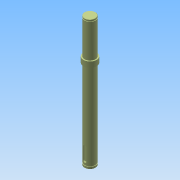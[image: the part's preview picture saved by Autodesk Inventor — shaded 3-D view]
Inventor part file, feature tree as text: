
AUTODESK INVENTOR PART (.ipt)
format: ipt  version: 2015 (Build 190159000, 159)  size: 131,072 bytes
history: native  units: mm
features: sketch x5, extrude x3, plane x2, revolve x2, chamfer x2
ambient origin geometry x8: Origin, YZ Plane, XZ Plane, XY Plane, X Axis, Y Axis, Z Axis, Center Point
bodies: 实体1 (feature_tree)
feature tree (14):
  extrude  "拉伸1"  Depth=237.2mm TaperAngle=0.0deg
  plane  "工作平面1"
  extrude  "拉伸2"  Depth=22.0mm
  revolve  "旋转1"  [1 undecoded]
  chamfer  "倒角1"  Distance=1.2mm
  plane  "工作平面2"
  extrude  "拉伸3"  Depth=9.175mm
  chamfer  "倒角2"  Distance=7.007942mm
  revolve  "旋转2"  Angle=90.0deg
  sketch  "草图1"  dims[d0=20.0mm d1=237.2mm d2=0.0mm]
  sketch  "草图2"  dims[d3=6.0mm d4=22.0mm]
  sketch  "草图3"  dims[d5=11.7mm d6=2.5mm d7=0.0mm]
  sketch  "草图4"  dims[d8=12.502001mm]
  sketch  "草图5"  dims[d9=4.0mm d10=1.2mm d11=9.175mm d12=7.007942mm d13=90.0deg d14=0.5mm d15=2.0mm d16=45.0deg d17=-162.2mm d18=24.0mm d19=10.0mm d20=0.0mm d21=0.5mm d22=2.0mm d23=45.0deg d24=1.2mm d25=2.3mm d26=3.771868mm d27=12.0mm d29=9.175mm d30=90.0deg]
note: 1 required parameter value undecoded (feature->parameter linkage not recoverable at this tier; creation-order binding heuristic only, values carry confidence <= 0.55)
